# Revit family: Air-Curtain_Climate-Control_PoweredAire_TIG-1Heater
name_source: partatom
category: Mechanical Equipment
units: mm (PartAtom-declared; Revit-internal decimal feet)

## family parameters
Classification Number = 23.75.35.17.21
Cut with Voids When Loaded = No
Host = Face
Maintain Annotation Orientation = No
Part Type = Normal
Room Calculation Point = No
Round Connector Dimension = Use Diameter
Shared = No

## types (7) — shared parameters
Assembly Code = D3090400
Construction Details = http://www.arcat.com
Default Elevation = 0' - 0"
Green Building-LEED = http://www.arcat.com
HVAC_Primary CFM = 0 CFM
Heating Element Load = 0 W
Keynote = 23 34 33
Manufacturer = Powered Aire, Inc
Manufacturer Fax = 724-588-3371
Manufacturer Website = http://www.poweredaire.com
Max Height = 12' - 0"
Motor HP = 0.75
Motor RPM = 1630
Overall Depth = 6' - 0 3/4"
Power Rating = 0 W
Product Data = http://www.arcat.com
Revision = R1_2016-08
Sales Information = http://www.poweredaire.com
Specification = http://www.arcat.com
Standards Conformance = ETL  ;  Made in USA
URL = http://www.poweredaire.com
Unit Depth = 1' - 8 1/4"
Unit Height = 1' - 4 3/4"
Unit Width Notes = Other Widths available.
zero-valued in all types: Expected Lifespan (Years), Heater Weight, Maintenance Schedule (Months), Warranty Duration (Years)

## per-type parameters (varying)
| type | Description | Exhaust Connection Diameter | HVAC_BTU Input | HVAC_BTU Output | HVAC_Outlet Velocity | HVAC_Outlet Velocity Uniformity | HVAC_Outlet Volume | HVAC_Temperature Rise | Heater Hanging Width | Model | Motor Count | Mounting Width | Nozzle Width | Sound Pressure | Unit Weight | Unit Width |
| 108'' Nozzle | Powered Aire Indirect Gas Heated Climate Control Air Curtain - TIG-3-108 as Specified | 0' - 6" | 105000.0 Btu/h | 280000.0 Btu/h | 3700 FPM | 0.92 | 7600 CFM | 34 °F | 4' - 0 5/8" | TIG-3-108 | 3 | 9' - 1 21/32" | 9' - 0 5/32" | >63 dBA | 640 | 9' - 3 5/32" |
| 96'' Nozzle | Powered Aire Indirect Gas Heated Climate Control Air Curtain - TIG-2-96 as Specified | 0' - 5" | 50000.0 Btu/h | 200000.0 Btu/h | 2800 FPM | 0.92 | 5100 CFM | 36 °F | 2' - 6 5/8" | TIG-2-96 | 2 | 8' - 1 9/16" | 8' - 0 1/16" | >63 dBA | 570 | 8' - 3 1/16" |
| 84'' Nozzle | Powered Aire Indirect Gas Heated Climate Control Air Curtain - TIG-2-84 as Specified | 0' - 5" | 50000.0 Btu/h | 200000.0 Btu/h | 3200 FPM | 0.93 | 5100 CFM | 37 °F | 2' - 6 5/8" | TIG-2-84 | 2 | 7' - 1 9/16" | 7' - 0 1/16" | >63 dBA | 530 | 7' - 3 1/16" |
| 72'' Nozzle | Powered Aire Indirect Gas Heated Climate Control Air Curtain - TIG-2-72 as Specified | 0' - 5" | 50000.0 Btu/h | 200000.0 Btu/h | 3700 FPM | 0.95 | 5100 CFM | 36 °F | 2' - 6 5/8" | TIG-2-72 | 2 | 6' - 1 9/16" | 6' - 0 1/16" | >63 dBA | 500 | 6' - 3 1/16" |
| 60'' Nozzle | Powered Aire Indirect Gas Heated Climate Control Air Curtain - TIG-1-60 as Specified | 0' - 5" | 150000.0 Btu/h | 120000.0 Btu/h | 2200 FPM | 0.91 | 2500 CFM | 44 °F | 1' - 6 5/8" | TIG-1-60 | 1 | 5' - 1 1/2" | 5' - 0" | 63 dBA | 340 | 5' - 3" |
| 48'' Nozzle | Powered Aire Indirect Gas Heated Climate Control Air Curtain - TIG-1-48 as Specified | 0' - 5" | 150000.0 Btu/h | 120000.0 Btu/h | 2800 FPM | 0.92 | 2600 CFM | 43 °F | 1' - 6 5/8" | TIG-1-48 | 1 | 4' - 1 1/2" | 4' - 0" | 63 dBA | 280 | 4' - 3" |
| 36'' Nozzle | Powered Aire Indirect Gas Heated Climate Control Air Curtain - TIG-1-36 as Specified | 0' - 5" | 150000.0 Btu/h | 120000.0 Btu/h | 3700 FPM | 0.95 | 2500 CFM | 44 °F | 1' - 6 5/8" | TIG-1-36 | 1 | 3' - 1 1/2" | 3' - 0" | 63 dBA | 250 | 3' - 3" |

## geometry (parser evidence)
native form markers: Sweep x7
no freeform markers — native parametric forms only
